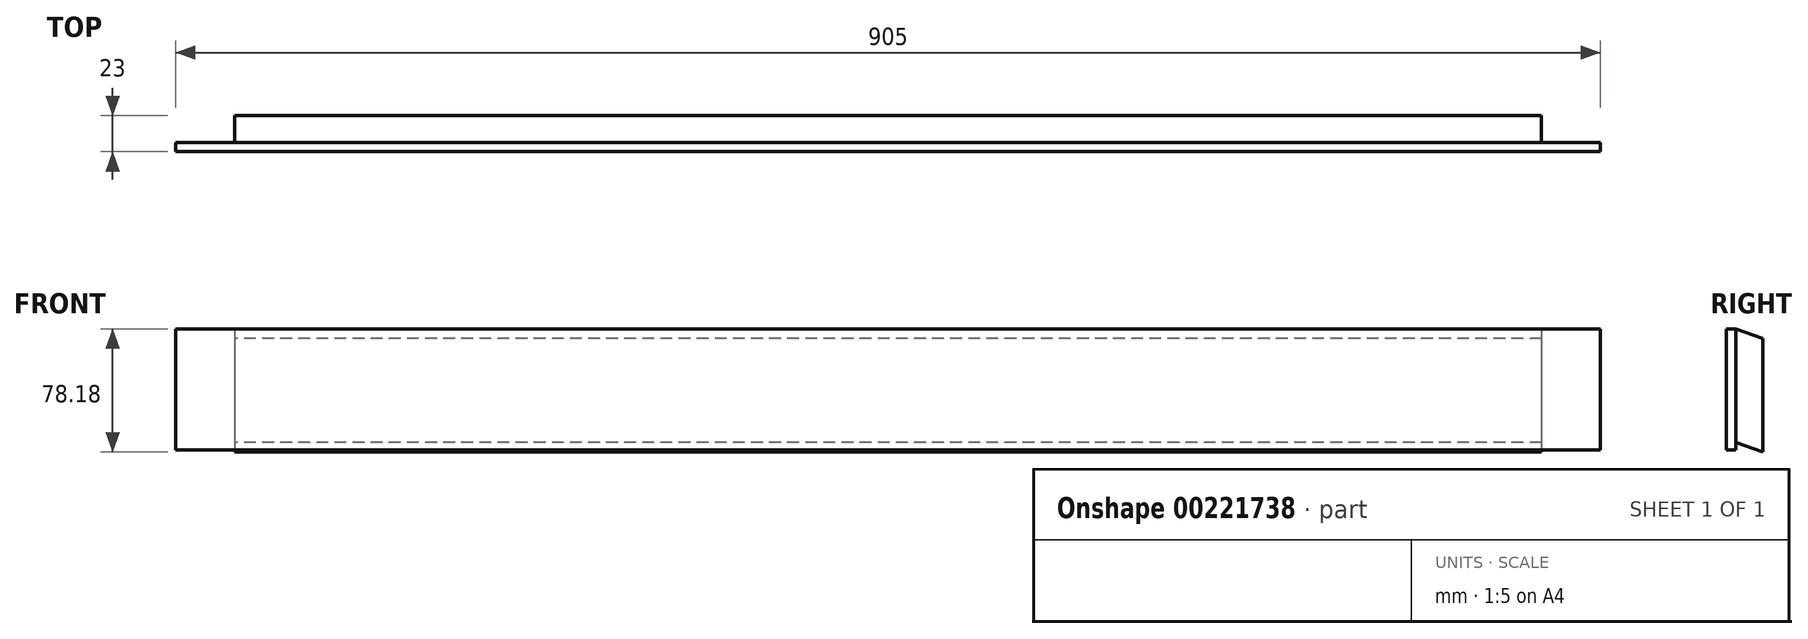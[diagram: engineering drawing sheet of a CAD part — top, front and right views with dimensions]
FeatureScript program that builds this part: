
annotation { "Feature Type Name" : "Feature", "Feature Type Description" : "" }
export const myFeature = defineFeature(function(context is Context, id is Id, definition is map)
    precondition{}
    {
        {
            var Q0;
            Q0=qCreatedBy(makeId("Right.planeOp"),FACE);
            var sketch = newSketch(context, id + "F0", { "sketchPlane" : qUnion([Q0])});
            skLineSegment(sketch, "E0.bottom", {"start": v(-8.5, 39.1) * mm, "end": v(8.5, 32.9) * mm});
            skLineSegment(sketch, "E0.top", {"start": v(-8.5, -32.9) * mm, "end": v(8.5, -39.1) * mm});
            skLineSegment(sketch, "E0.left", {"start": v(-8.5, 39.1) * mm, "end": v(-8.5, -32.9) * mm});
            skLineSegment(sketch, "E0.right", {"start": v(8.5, 32.9) * mm, "end": v(8.5, -39.1) * mm});
            skPoint(sketch, "E0.middle", {"position": v(0, 0) * mm});
            skSolve(sketch);
        }
        {
            var Q0;
            Q0 = qSketchRegion(id + "F0", true);
            extrude(context, id + "F1", {"entities" : qUnion([Q0]), "depth" : 830 * mm});
        }
        {
            var Q0;
            Q0=makeQuery(id+"F1.opExtrude","SWEPT_FACE",FACE,{"disambiguationData":[OSD([sQuery(id+"F0.wireOp",EDGE,"E0.left")])]});
            var sketch = newSketch(context, id + "F2", { "sketchPlane" : qUnion([Q0])});
            skLineSegment(sketch, "E1.0", {"start": v(867.5, 39.1) * mm, "end": v(-37.5, 39.1) * mm});
            skLineSegment(sketch, "E2", {"start": v(867.5, 39.1) * mm, "end": v(867.5, -37.9) * mm});
            skLineSegment(sketch, "E3", {"start": v(867.5, -37.9) * mm, "end": v(-37.5, -37.9) * mm});
            skLineSegment(sketch, "E4", {"start": v(-37.5, -64.88) * mm, "end": v(-37.5, 39.1) * mm});
            skPoint(sketch, "E5.orphan", {"position": v(830, 39.1) * mm});
            skSolve(sketch);
        }
        {
            var Q0;
            Q0 = qSketchRegion(id + "F2", true);
            extrude(context, id + "F3", {"entities" : qUnion([Q0]), "operationType" : NewBodyOperationType.ADD, "depth" : 6 * mm});
        }
    });
